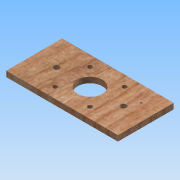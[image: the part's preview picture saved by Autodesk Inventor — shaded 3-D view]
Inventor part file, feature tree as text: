
AUTODESK INVENTOR PART (.ipt)
format: ipt  version: 2015 (Build 190159000, 159)  size: 249,856 bytes
history: native  units: mm
features: other x9, sketch x9, extrude x3, hole x3
ambient origin geometry x8: Origin, YZ Plane, XZ Plane, XY Plane, X Axis, Y Axis, Z Axis, Center Point
bodies: Body1 (feature_tree)
feature tree (24):
  other  "Blocks"
  extrude  "Extrusion2"  Depth=50.0mm
  hole  "Hole4"  [1 undecoded]
  hole  "Hole5"  [1 undecoded]
  hole  "Hole8"  [1 undecoded]
  extrude  "Extrusion5"  Depth=20.0mm
  extrude  "Extrusion6"  TaperAngle=0.0deg  [1 undecoded]
  sketch  "Sketch42"  dims[d129=5.5mm d130=0.0mm]
  sketch  "Sketch43"  dims[d131=5.5mm d132=10.0mm d133=8.333333mm d134=5.5mm d135=0.0mm d29=1.0mm d30=1.0mm]
  sketch  "Sketch41"  dims[d122=5.5mm d123=20.0mm]
  sketch  "Sketch10"  dims[d21=100.0mm d22=50.0mm]
  sketch  "Sketch13"  dims[d23=5.0mm d24=0.0mm d43=31.0mm]
  sketch  "Sketch16"  dims[d44=31.0mm]
  sketch  "Sketch17"  dims[d45=4.0mm d46=6.0mm d47=4.0mm d48=2.0mm d49=90.0deg d50=4.0mm d51=0.0mm d52=60.0mm]
  sketch  "Sketch33"  dims[d53=5.2mm d54=6.0mm d55=4.0mm d56=2.0mm d57=90.0deg d58=4.0mm d59=0.0mm]
  sketch  "Sketch34"  dims[d78=22.0mm d79=6.0mm d80=4.0mm d81=2.0mm d82=90.0deg d83=2.0mm d84=0.0mm d121=20.0mm]
  other  "Block1"
  other  "Block2"
  other  "Block3"
  other  "Block4"
  other  "Block3:1"
  other  "Block3:2"
  other  "Block4:1"
  other  "Block4:2"
note: 4 required parameter values undecoded (feature->parameter linkage not recoverable at this tier; creation-order binding heuristic only, values carry confidence <= 0.55)
